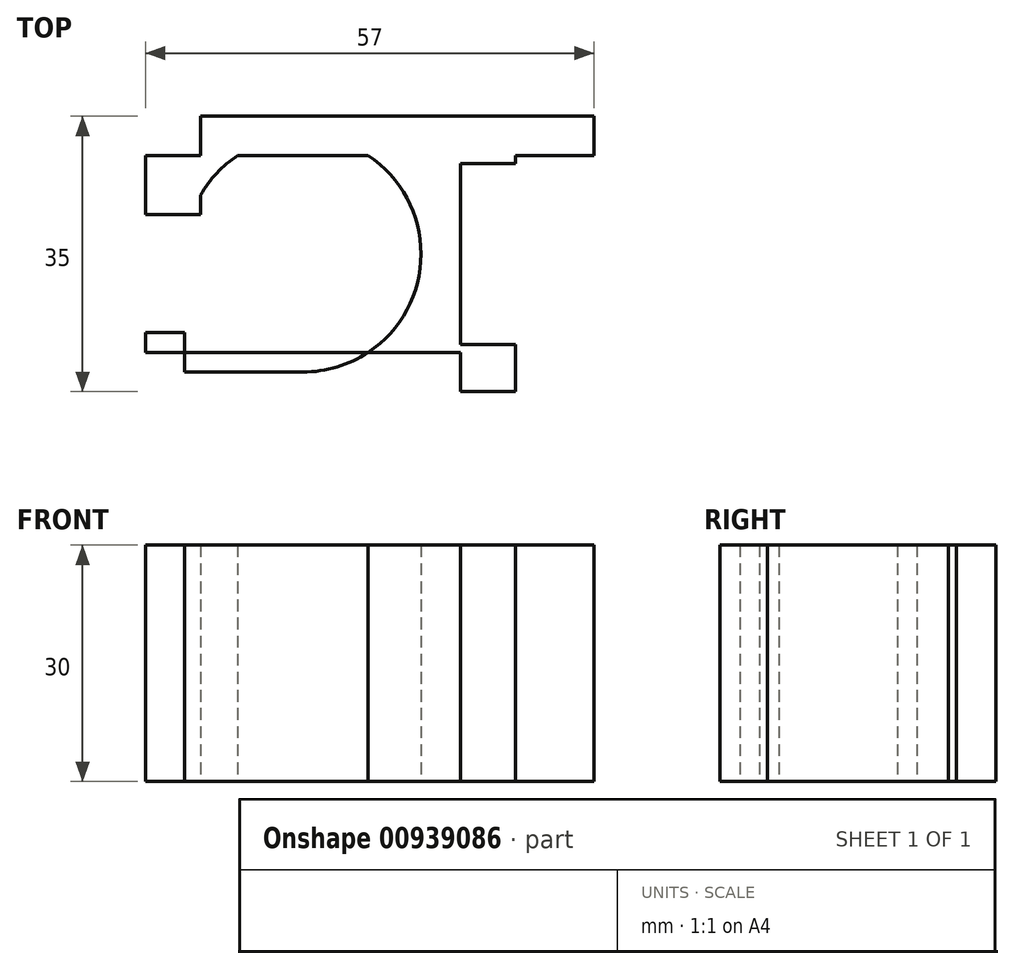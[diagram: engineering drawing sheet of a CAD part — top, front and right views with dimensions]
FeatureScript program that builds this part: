
annotation { "Feature Type Name" : "Feature", "Feature Type Description" : "" }
export const myFeature = defineFeature(function(context is Context, id is Id, definition is map)
    precondition{}
    {
        {
            var Q0;
            Q0=qCreatedBy(makeId("Top.planeOp"),FACE);
            var sketch = newSketch(context, id + "F0", { "sketchPlane" : qUnion([Q0])});
            skLineSegment(sketch, "E0.bottom", {"start": v(20, 17.5) * mm, "end": v(-20, 17.5) * mm});
            skLineSegment(sketch, "E0.top", {"start": v(20, -17.5) * mm, "end": v(-20, -17.5) * mm});
            skLineSegment(sketch, "E0.left", {"start": v(20, 17.5) * mm, "end": v(20, -17.5) * mm});
            skLineSegment(sketch, "E0.right", {"start": v(-20, 17.5) * mm, "end": v(-20, -17.5) * mm});
            skPoint(sketch, "E0.middle", {"position": v(0, 0) * mm});
            skCircle(sketch, "E1", {"center": v(0, 0) * mm, "radius": 15 * mm});
            skLineSegment(sketch, "E2.bottom", {"start": v(-20, 17.5) * mm, "end": v(20, 17.5) * mm});
            skLineSegment(sketch, "E2.top", {"start": v(-20, 12.5) * mm, "end": v(20, 12.5) * mm});
            skLineSegment(sketch, "E2.left", {"start": v(-20, 17.5) * mm, "end": v(-20, 12.5) * mm});
            skLineSegment(sketch, "E2.right", {"start": v(20, 17.5) * mm, "end": v(20, 12.5) * mm});
            skLineSegment(sketch, "E3.bottom", {"start": v(-20, -17.5) * mm, "end": v(20, -17.5) * mm});
            skLineSegment(sketch, "E3.top", {"start": v(-20, -12.5) * mm, "end": v(20, -12.5) * mm});
            skLineSegment(sketch, "E3.left", {"start": v(-20, -17.5) * mm, "end": v(-20, -12.5) * mm});
            skLineSegment(sketch, "E3.right", {"start": v(20, -17.5) * mm, "end": v(20, -12.5) * mm});
            skLineSegment(sketch, "E4.bottom", {"start": v(-20, 17.5) * mm, "end": v(-13, 17.5) * mm});
            skLineSegment(sketch, "E4.top", {"start": v(-20, 5) * mm, "end": v(-13, 5) * mm});
            skLineSegment(sketch, "E4.left", {"start": v(-20, 17.5) * mm, "end": v(-20, 5) * mm});
            skLineSegment(sketch, "E4.right", {"start": v(-13, 17.5) * mm, "end": v(-13, 5) * mm});
            skLineSegment(sketch, "E5.bottom", {"start": v(-20, -17.5) * mm, "end": v(-15, -17.5) * mm});
            skLineSegment(sketch, "E5.top", {"start": v(-20, -10) * mm, "end": v(-15, -10) * mm});
            skLineSegment(sketch, "E5.left", {"start": v(-20, -17.5) * mm, "end": v(-20, -10) * mm});
            skLineSegment(sketch, "E5.right", {"start": v(-15, -17.5) * mm, "end": v(-15, -10) * mm});
            skLineSegment(sketch, "E6", {"start": v(0, -15) * mm, "end": v(-15, -15) * mm});
            skLineSegment(sketch, "E7.bottom", {"start": v(20, -17.5) * mm, "end": v(27, -17.5) * mm});
            skLineSegment(sketch, "E7.top", {"start": v(20, 17.5) * mm, "end": v(27, 17.5) * mm});
            skLineSegment(sketch, "E7.left", {"start": v(20, -17.5) * mm, "end": v(20, 17.5) * mm});
            skLineSegment(sketch, "E7.right", {"start": v(27, -17.5) * mm, "end": v(27, 17.5) * mm});
            skLineSegment(sketch, "E8.bottom", {"start": v(20, -12.5) * mm, "end": v(27, -12.5) * mm});
            skLineSegment(sketch, "E8.top", {"start": v(20, 12.5) * mm, "end": v(27, 12.5) * mm});
            skLineSegment(sketch, "E8.left", {"start": v(20, -12.5) * mm, "end": v(20, 12.5) * mm});
            skLineSegment(sketch, "E8.right", {"start": v(27, -12.5) * mm, "end": v(27, 12.5) * mm});
            skLineSegment(sketch, "E9.bottom", {"start": v(27, 17.5) * mm, "end": v(37, 17.5) * mm});
            skLineSegment(sketch, "E9.top", {"start": v(27, 12.5) * mm, "end": v(37, 12.5) * mm});
            skLineSegment(sketch, "E9.left", {"start": v(27, 17.5) * mm, "end": v(27, 12.5) * mm});
            skLineSegment(sketch, "E9.right", {"start": v(37, 17.5) * mm, "end": v(37, 12.5) * mm});
            skLineSegment(sketch, "E10.top", {"start": v(20, 11.5) * mm, "end": v(27, 11.5) * mm});
            skLineSegment(sketch, "E10.left", {"start": v(20, 12.5) * mm, "end": v(20, 11.5) * mm});
            skLineSegment(sketch, "E10.right", {"start": v(27, 12.5) * mm, "end": v(27, 11.5) * mm});
            skLineSegment(sketch, "E11.top", {"start": v(20, -11.5) * mm, "end": v(27, -11.5) * mm});
            skLineSegment(sketch, "E11.left", {"start": v(20, -12.5) * mm, "end": v(20, -11.5) * mm});
            skLineSegment(sketch, "E11.right", {"start": v(27, -12.5) * mm, "end": v(27, -11.5) * mm});
            skSolve(sketch);
        }
        {
            var Q0;
            {var subQ0=sQuery(id+"F0.wireOp",EDGE,"E2.top");var subQ1=sQuery(id+"F0.wireOp",EDGE,"E1");var subQ2=makeQuery(id+"F0.imprint","INTERSECT",VERTEX,{"disambiguationData":[OD(1.0)],"derivedFrom":[subQ1,subQ0]});Q0=makeQuery(id+"F0.imprint","IMPRINT",FACE,{"disambiguationData":[TD([[makeQuery(id+"F0.imprint","IMPRINT",EDGE,{"disambiguationData":[TD([[subQ2,-1.0]])],"derivedFrom":subQ1}),1.0]])]});}
            var Q1;
            {var subQ0=sQuery(id+"F0.wireOp",EDGE,"E0.left");Q1=makeQuery(id+"F0.imprint","IMPRINT",FACE,{"disambiguationData":[TD([[makeQuery(id+"F0.imprint","IMPRINT",EDGE,{"derivedFrom":subQ0}),-1.0]])]});}
            var Q2;
            {var subQ6=sQuery(id+"F0.wireOp",EDGE,"E2.bottom");Q2=makeQuery(id+"F0.imprint","IMPRINT",FACE,{"disambiguationData":[TD([[makeQuery(id+"F0.imprint","IMPRINT",EDGE,{"derivedFrom":subQ6}),-1.0]])]});}
            var Q3;
            {var subQ0=sQuery(id+"F0.wireOp",EDGE,"E4.bottom");Q3=makeQuery(id+"F0.imprint","IMPRINT",FACE,{"disambiguationData":[TD([[makeQuery(id+"F0.imprint","IMPRINT",EDGE,{"derivedFrom":subQ0}),-1.0]])]});}
            var Q4;
            {var subQ0=sQuery(id+"F0.wireOp",EDGE,"E2.top");var subQ1=sQuery(id+"F0.wireOp",EDGE,"E1");var subQ2=makeQuery(id+"F0.imprint","INTERSECT",VERTEX,{"disambiguationData":[OD(1.0)],"derivedFrom":[subQ1,subQ0]});Q4=makeQuery(id+"F0.imprint","IMPRINT",FACE,{"disambiguationData":[TD([[makeQuery(id+"F0.imprint","IMPRINT",EDGE,{"disambiguationData":[TD([[subQ2,-1.0]])],"derivedFrom":subQ1}),-1.0]])]});}
            var Q5;
            Q5=makeQuery(id+"F0.imprint","IMPRINT",FACE,{"disambiguationData":[TD([[makeQuery(id+"F0.imprint","IMPRINT",EDGE,{"derivedFrom":sQuery(id+"F0.wireOp",EDGE,"E3.bottom")}),1.0]])]});
            var Q6;
            {var subQ3=sQuery(id+"F0.wireOp",EDGE,"E1");var subQ7=sQuery(id+"F0.wireOp",EDGE,"E4.right");var subQ9=makeQuery(id+"F0.imprint","INTERSECT",VERTEX,{"derivedFrom":[subQ3,subQ7]});Q6=makeQuery(id+"F0.imprint","IMPRINT",FACE,{"disambiguationData":[TD([[makeQuery(id+"F0.imprint","IMPRINT",EDGE,{"disambiguationData":[TD([[subQ9,-1.0]])],"derivedFrom":subQ3}),-1.0]])]});}
            var Q7;
            {var subQ0=sQuery(id+"F0.wireOp",EDGE,"E2.top");var subQ1=sQuery(id+"F0.wireOp",EDGE,"E1");var subQ2=makeQuery(id+"F0.imprint","INTERSECT",VERTEX,{"disambiguationData":[OD(0.0)],"derivedFrom":[subQ1,subQ0]});Q7=makeQuery(id+"F0.imprint","IMPRINT",FACE,{"disambiguationData":[TD([[makeQuery(id+"F0.imprint","IMPRINT",EDGE,{"disambiguationData":[TD([[subQ2,-1.0]])],"derivedFrom":subQ1}),-1.0]])]});}
            var Q8;
            {var subQ1=sQuery(id+"F0.wireOp",EDGE,"E5.bottom");Q8=makeQuery(id+"F0.imprint","IMPRINT",FACE,{"disambiguationData":[TD([[makeQuery(id+"F0.imprint","IMPRINT",EDGE,{"derivedFrom":subQ1}),1.0]])]});}
            var Q9;
            {var subQ5=sQuery(id+"F0.wireOp",EDGE,"E5.top");Q9=makeQuery(id+"F0.imprint","IMPRINT",FACE,{"disambiguationData":[TD([[makeQuery(id+"F0.imprint","IMPRINT",EDGE,{"derivedFrom":subQ5}),-1.0]])]});}
            var Q10;
            Q10=makeQuery(id+"F0.imprint","IMPRINT",FACE,{"disambiguationData":[TD([[makeQuery(id+"F0.imprint","IMPRINT",EDGE,{"derivedFrom":sQuery(id+"F0.wireOp",EDGE,"E8.bottom")}),1.0]])]});
            var Q11;
            {var subQ0=sQuery(id+"F0.wireOp",EDGE,"E7.bottom");Q11=makeQuery(id+"F0.imprint","IMPRINT",FACE,{"disambiguationData":[TD([[makeQuery(id+"F0.imprint","IMPRINT",EDGE,{"derivedFrom":subQ0}),1.0]])]});}
            var Q12;
            {var subQ0=sQuery(id+"F0.wireOp",EDGE,"E7.top");Q12=makeQuery(id+"F0.imprint","IMPRINT",FACE,{"disambiguationData":[TD([[makeQuery(id+"F0.imprint","IMPRINT",EDGE,{"derivedFrom":subQ0}),-1.0]])]});}
            var Q13;
            Q13=makeQuery(id+"F0.imprint","IMPRINT",FACE,{"disambiguationData":[TD([[makeQuery(id+"F0.imprint","IMPRINT",EDGE,{"derivedFrom":sQuery(id+"F0.wireOp",EDGE,"E8.top")}),-1.0]])]});
            var Q14;
            Q14=makeQuery(id+"F0.imprint","IMPRINT",FACE,{"disambiguationData":[TD([[makeQuery(id+"F0.imprint","IMPRINT",EDGE,{"derivedFrom":sQuery(id+"F0.wireOp",EDGE,"E9.bottom")}),-1.0]])]});
            var Q15;
            Q15=makeQuery(id+"F0.imprint","IMPRINT",FACE,{"disambiguationData":[TD([[makeQuery(id+"F0.imprint","IMPRINT",EDGE,{"derivedFrom":sQuery(id+"F0.wireOp",EDGE,"E8.left")}),1.0]])]});
            var Q16;
            {var subQ0=sQuery(id+"F0.wireOp",EDGE,"E4.right");var subQ1=sQuery(id+"F0.wireOp",EDGE,"E1");var subQ2=makeQuery(id+"F0.imprint","INTERSECT",VERTEX,{"derivedFrom":[subQ1,subQ0]});Q16=makeQuery(id+"F0.imprint","IMPRINT",FACE,{"disambiguationData":[TD([[makeQuery(id+"F0.imprint","IMPRINT",EDGE,{"disambiguationData":[TD([[subQ2,-1.0]])],"derivedFrom":subQ1}),1.0]])]});}
            var Q17;
            {var subQ0=sQuery(id+"F0.wireOp",EDGE,"E6");Q17=makeQuery(id+"F0.imprint","IMPRINT",FACE,{"disambiguationData":[TD([[makeQuery(id+"F0.imprint","IMPRINT",EDGE,{"derivedFrom":subQ0}),-1.0]])]});}
            var Q18;
            {var subQ0=sQuery(id+"F0.wireOp",EDGE,"E1");var subQ1=makeQuery(id+"F0.imprint","INTERSECT",VERTEX,{"derivedFrom":[subQ0,sQuery(id+"F0.wireOp",EDGE,"E6")]});Q18=makeQuery(id+"F0.imprint","IMPRINT",FACE,{"disambiguationData":[TD([[makeQuery(id+"F0.imprint","IMPRINT",EDGE,{"disambiguationData":[TD([[subQ1,1.0]])],"derivedFrom":subQ0}),1.0]])]});}
            extrude(context, id + "F1", {"entities" : qUnion([Q0, Q1, Q2, Q3, Q4, Q5, Q6, Q7, Q8, Q9, Q10, Q11, Q12, Q13, Q14, Q15, Q16, Q17, Q18]), "depth" : 30 * mm, "offsetDistance" : 25.4 * mm});
        }
    });
